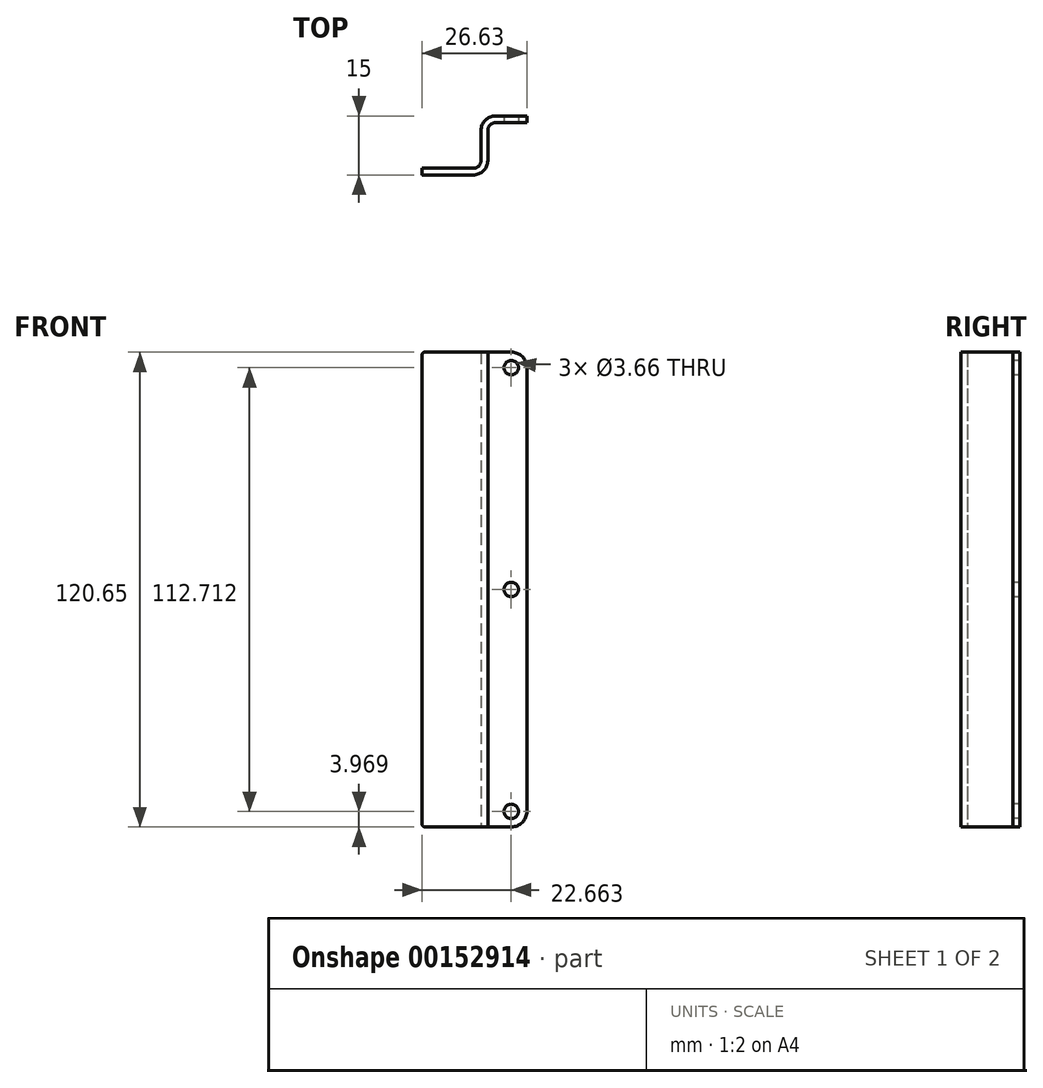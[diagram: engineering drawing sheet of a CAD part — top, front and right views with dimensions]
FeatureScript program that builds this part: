
annotation { "Feature Type Name" : "Feature", "Feature Type Description" : "" }
export const myFeature = defineFeature(function(context is Context, id is Id, definition is map)
    precondition{}
    {
        {
            var Q0;
            Q0=qCreatedBy(makeId("Top.planeOp"),FACE);
            var sketch = newSketch(context, id + "F0", { "sketchPlane" : qUnion([Q0])});
            skLineSegment(sketch, "E0.left", {"start": v(0, 0) * mm, "end": v(0, -13.3) * mm});
            skLineSegment(sketch, "E0.right", {"start": v(-1.7, 1.7) * mm, "end": v(-1.7, -11.58) * mm});
            skLineSegment(sketch, "E1.bottom", {"start": v(-1.7, -11.58) * mm, "end": v(-16.7, -11.58) * mm});
            skLineSegment(sketch, "E1.top", {"start": v(0, -13.3) * mm, "end": v(-16.7, -13.3) * mm});
            skLineSegment(sketch, "E1.right", {"start": v(-16.7, -11.58) * mm, "end": v(-16.7, -13.3) * mm});
            skLineSegment(sketch, "E2.bottom", {"start": v(0, 0) * mm, "end": v(9.92, 0) * mm});
            skLineSegment(sketch, "E2.top", {"start": v(-1.7, 1.7) * mm, "end": v(9.92, 1.7) * mm});
            skLineSegment(sketch, "E2.right", {"start": v(9.92, 0) * mm, "end": v(9.92, 1.7) * mm});
            skLineSegment(sketch, "E3", {"start": v(0, -6.65) * mm, "end": v(-1.7, -6.65) * mm, "construction": true});
            skSolve(sketch);
        }
        {
            var Q0;
            Q0 = qSketchRegion(id + "F0", true);
            extrude(context, id + "F1", {"entities" : qUnion([Q0]), "depth" : 120.65 * mm});
        }
        {
            var Q0;
            Q0=makeQuery(id+"F1.opExtrude","SWEPT_EDGE",EDGE,{"disambiguationData":[OSD([sQuery(id+"F0.wireOp",EDGE,"E0.left"),sQuery(id+"F0.wireOp",EDGE,"E2.bottom")])]});
            var Q1;
            Q1=makeQuery(id+"F1.opExtrude","SWEPT_EDGE",EDGE,{"disambiguationData":[OSD([sQuery(id+"F0.wireOp",EDGE,"E0.right"),sQuery(id+"F0.wireOp",EDGE,"E1.bottom")])]});
            fillet(context, id + "F2", {"entities" : qUnion([Q0, Q1]), "radius" : 1.98 * mm, "tangentPropagation" : true, "allowEdgeOverflow" : false});
        }
        {
            var Q0;
            Q0=makeQuery(id+"F1.opExtrude","SWEPT_EDGE",EDGE,{"disambiguationData":[OSD([sQuery(id+"F0.wireOp",EDGE,"E0.left"),sQuery(id+"F0.wireOp",EDGE,"E1.top")])]});
            var Q1;
            Q1=makeQuery(id+"F1.opExtrude","SWEPT_EDGE",EDGE,{"disambiguationData":[OSD([sQuery(id+"F0.wireOp",EDGE,"E0.right"),sQuery(id+"F0.wireOp",EDGE,"E2.top")])]});
            fillet(context, id + "F3", {"entities" : qUnion([Q0, Q1]), "radius" : 3.7 * mm, "tangentPropagation" : true, "allowEdgeOverflow" : false});
        }
        {
            var Q0;
            Q0=makeQuery(id+"F1.opExtrude","CAP_EDGE",EDGE,{"disambiguationData":[OSD([sQuery(id+"F0.wireOp",EDGE,"E2.right")])],"isStart":false});
            var Q1;
            Q1=makeQuery(id+"F1.opExtrude","CAP_EDGE",EDGE,{"disambiguationData":[OSD([sQuery(id+"F0.wireOp",EDGE,"E2.right")])],"isStart":true});
            fillet(context, id + "F4", {"entities" : qUnion([Q0, Q1]), "radius" : 3.97 * mm, "tangentPropagation" : true, "allowEdgeOverflow" : false});
        }
        {
            var Q0;
            Q0=makeQuery(id+"F1.opExtrude","CAP_EDGE",EDGE,{"disambiguationData":[OSD([sQuery(id+"F0.wireOp",EDGE,"E1.right")])],"isStart":true});
            var Q1;
            Q1=makeQuery(id+"F1.opExtrude","CAP_EDGE",EDGE,{"disambiguationData":[OSD([sQuery(id+"F0.wireOp",EDGE,"E1.right")])],"isStart":false});
            fillet(context, id + "F5", {"entities" : qUnion([Q0, Q1]), "radius" : 0.76 * mm, "tangentPropagation" : true, "allowEdgeOverflow" : false});
        }
        {
            var Q0;
            Q0=makeQuery(id+"F1.opExtrude","SWEPT_FACE",FACE,{"disambiguationData":[OSD([sQuery(id+"F0.wireOp",EDGE,"E2.bottom")])]});
            var sketch = newSketch(context, id + "F6", { "sketchPlane" : qUnion([Q0])});
            skCircle(sketch, "E4", {"center": v(5.95, 116.68) * mm, "radius": 1.83 * mm});
            skCircle(sketch, "E5", {"center": v(5.95, 3.97) * mm, "radius": 1.83 * mm});
            skLineSegment(sketch, "E6", {"start": v(5.95, 3.97) * mm, "end": v(5.95, 116.68) * mm, "construction": true});
            skCircle(sketch, "E7", {"center": v(5.95, 60.33) * mm, "radius": 1.83 * mm});
            skSolve(sketch);
        }
        {
            var Q0;
            Q0 = qSketchRegion(id + "F6", true);
            var Q1;
            Q1=makeQuery(id+"F1.opExtrude","SWEPT_FACE",FACE,{"disambiguationData":[OSD([sQuery(id+"F0.wireOp",EDGE,"E2.top")])]});
            extrude(context, id + "F7", {"entities" : qUnion([Q0]), "operationType" : NewBodyOperationType.REMOVE, "endBound" : BoundingType.UP_TO_SURFACE, "oppositeDirection" : true, "endBoundEntityFace" : qUnion([Q1]), "depth" : 25.4 * mm});
        }
    });
